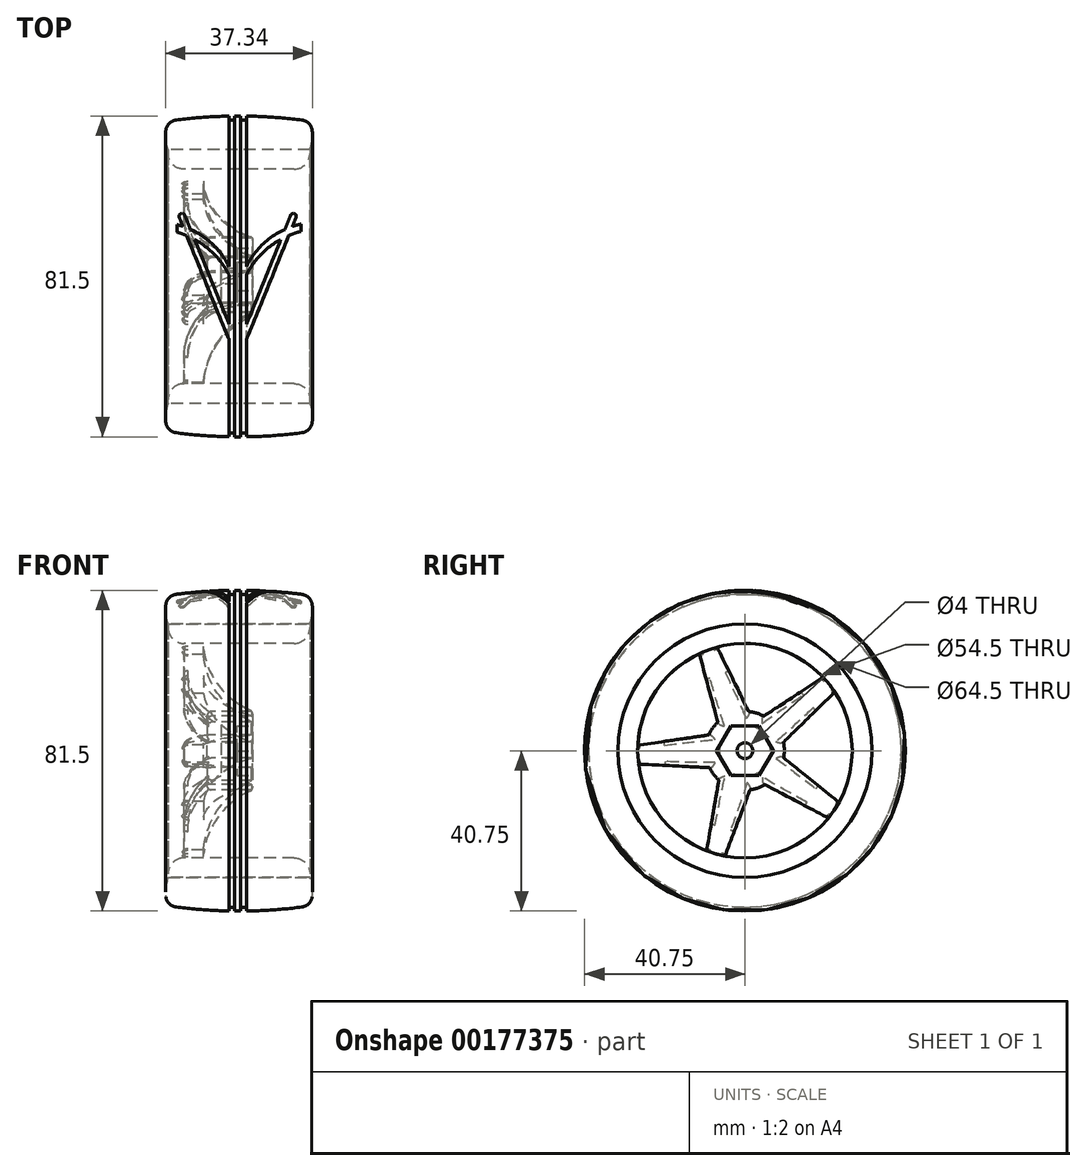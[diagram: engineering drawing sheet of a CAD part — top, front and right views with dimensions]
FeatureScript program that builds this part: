
annotation { "Feature Type Name" : "Feature", "Feature Type Description" : "" }
export const myFeature = defineFeature(function(context is Context, id is Id, definition is map)
    precondition{}
    {
        {
            var Q0;
            Q0=qCreatedBy(makeId("Front.planeOp"),FACE);
            var sketch = newSketch(context, id + "F0", { "sketchPlane" : qUnion([Q0])});
            skLineSegment(sketch, "E0", {"start": v(0, 0) * mm, "end": v(0, 27.25) * mm, "construction": true});
            skLineSegment(sketch, "E1", {"start": v(0, 27.25) * mm, "end": v(18.55, 27.25) * mm, "construction": true});
            skLineSegment(sketch, "E2", {"start": v(18.55, 27.25) * mm, "end": v(18.55, 32.25) * mm, "construction": true});
            skLineSegment(sketch, "E3", {"start": v(18.55, 32.25) * mm, "end": v(-17.45, 32.25) * mm, "construction": true});
            skLineSegment(sketch, "E4", {"start": v(-17.45, 32.25) * mm, "end": v(-17.45, 27.25) * mm, "construction": true});
            skLineSegment(sketch, "E5", {"start": v(-17.45, 27.25) * mm, "end": v(-4, 27.25) * mm, "construction": true});
            skLineSegment(sketch, "E6", {"start": v(-4, 27.25) * mm, "end": v(-4, 0) * mm, "construction": true});
            skLineSegment(sketch, "E7", {"start": v(-4, 0) * mm, "end": v(0, 0) * mm, "construction": true});
            skSolve(sketch);
        }
        {
            var Q0;
            Q0=qCreatedBy(makeId("Front.planeOp"),FACE);
            var sketch = newSketch(context, id + "F1", { "sketchPlane" : qUnion([Q0])});
            skLineSegment(sketch, "E8", {"start": v(-20, 0) * mm, "end": v(20, 0) * mm, "construction": true});
            skLineSegment(sketch, "E9", {"start": v(-4, 2) * mm, "end": v(0, 2) * mm});
            skLineSegment(sketch, "E10", {"start": v(0, 2) * mm, "end": v(0, 6.5) * mm, "construction": true});
            skLineSegment(sketch, "E11", {"start": v(0, 6.5) * mm, "end": v(-4, 6.5) * mm, "construction": true});
            skLineSegment(sketch, "E12", {"start": v(-4, 6.5) * mm, "end": v(-4, 2) * mm});
            skLineSegment(sketch, "E13", {"start": v(-13.45, 27.25) * mm, "end": v(-13.45, 20.44) * mm});
            skArc(sketch, "E14", {"start": v(-13.45, 20.44) * mm, "mid": v(-10.86, 12.02) * mm, "end": v(-4, 6.5) * mm});
            skArc(sketch, "E15", {"start": v(-17.45, 31.25) * mm, "mid": v(-16.28, 28.42) * mm, "end": v(-13.45, 27.25) * mm});
            skLineSegment(sketch, "E16", {"start": v(-17.45, 31.25) * mm, "end": v(-17.45, 32.25) * mm});
            skLineSegment(sketch, "E17", {"start": v(-17.45, 32.25) * mm, "end": v(18.55, 32.25) * mm});
            skLineSegment(sketch, "E18", {"start": v(18.55, 32.25) * mm, "end": v(18.55, 31.25) * mm});
            skLineSegment(sketch, "E19", {"start": v(14.55, 27.25) * mm, "end": v(-8.45, 27.25) * mm});
            skArc(sketch, "E20", {"start": v(-8.45, 27.25) * mm, "mid": v(-4.9, 17.1) * mm, "end": v(3.4, 10.25) * mm});
            skPoint(sketch, "E21.visualSharp", {"position": v(18.55, 27.25) * mm});
            skArc(sketch, "E21.filletArc", {"start": v(14.55, 27.25) * mm, "mid": v(17.38, 28.42) * mm, "end": v(18.55, 31.25) * mm});
            skLineSegment(sketch, "E22", {"start": v(4, 9.34) * mm, "end": v(4, 3) * mm});
            skLineSegment(sketch, "E23", {"start": v(4, 3) * mm, "end": v(0, 3) * mm});
            skLineSegment(sketch, "E24", {"start": v(0, 3) * mm, "end": v(0, 2) * mm});
            skPoint(sketch, "E25.visualSharp", {"position": v(4, 10) * mm});
            skArc(sketch, "E25.filletArc", {"start": v(4, 9.34) * mm, "mid": v(3.84, 9.88) * mm, "end": v(3.4, 10.25) * mm});
            skSolve(sketch);
        }
        {
            var Q0;
            Q0=qSketchRegion(id+"F1",true);
            var Q1;
            Q1=sQuery(id+"F1.wireOp",EDGE,"E8");
            revolve(context, id + "F2", {"surfaceOperationType" : NewSurfaceOperationType.NEW, "entities" : qUnion([Q0]), "axis" : qUnion([Q1]), "revolveType" : RevolveType.FULL});
        }
        {
            var Q0;
            Q0=makeQuery(id+"F2.opRevolve","SWEPT_FACE",FACE,{"disambiguationData":[OSD([sQuery(id+"F1.wireOp",EDGE,"E22")])]});
            var sketch = newSketch(context, id + "F3", { "sketchPlane" : qUnion([Q0])});
            skCircle(sketch, "E26.cCircle", {"center": v(0, 0) * mm, "radius": 6.25 * mm, "construction": true});
            skLineSegment(sketch, "E26.0", {"start": v(-3.6, 6.25) * mm, "end": v(3.6, 6.25) * mm});
            skLineSegment(sketch, "E26.1", {"start": v(3.6, 6.25) * mm, "end": v(7.22, 0) * mm});
            skLineSegment(sketch, "E26.2", {"start": v(7.22, 0) * mm, "end": v(3.6, -6.25) * mm});
            skLineSegment(sketch, "E26.3", {"start": v(3.6, -6.25) * mm, "end": v(-3.6, -6.25) * mm});
            skLineSegment(sketch, "E26.4", {"start": v(-3.6, -6.25) * mm, "end": v(-7.22, 0) * mm});
            skLineSegment(sketch, "E26.5", {"start": v(-7.22, 0) * mm, "end": v(-3.6, 6.25) * mm});
            skPoint(sketch, "E26.0.midPoint", {"position": v(0, 6.25) * mm});
            skSolve(sketch);
        }
        {
            var Q0;
            Q0=qSketchRegion(id+"F3",true);
            var Q1;
            Q1=makeQuery(id+"F2.opRevolve","SWEPT_FACE",FACE,{"disambiguationData":[OSD([sQuery(id+"F1.wireOp",EDGE,"E24")])]});
            extrude(context, id + "F4", {"entities" : qUnion([Q0]), "operationType" : NewBodyOperationType.REMOVE, "endBound" : BoundingType.UP_TO_SURFACE, "oppositeDirection" : true, "depth" : 25 * mm, "endBoundEntityFace" : qUnion([Q1]), "offsetDistance" : 25 * mm});
        }
        {
            var Q0;
            Q0=makeQuery(id+"F2.opRevolve","SWEPT_FACE",FACE,{"disambiguationData":[OSD([sQuery(id+"F1.wireOp",EDGE,"E16")])]});
            var sketch = newSketch(context, id + "F5", { "sketchPlane" : qUnion([Q0])});
            skLineSegment(sketch, "E27", {"start": v(11.62, 24.65) * mm, "end": v(6.88, 7.26) * mm});
            skArc(sketch, "E28", {"start": v(9.17, 3.98) * mm, "mid": v(8.2, 5.74) * mm, "end": v(6.88, 7.26) * mm});
            skLineSegment(sketch, "E29", {"start": v(9.17, 3.98) * mm, "end": v(27.21, 1.4) * mm});
            skArc(sketch, "E30", {"start": v(27.21, 1.4) * mm, "mid": v(22.63, 15.18) * mm, "end": v(11.62, 24.65) * mm});
            skLineSegment(sketch, "E31", {"start": v(0, 0) * mm, "end": v(22.32, 15.63) * mm, "construction": true});
            skLineSegment(sketch, "E32.1.0", {"start": v(-19.85, 18.66) * mm, "end": v(-4.78, 8.79) * mm});
            skArc(sketch, "E32.1.1", {"start": v(7.08, 26.31) * mm, "mid": v(-7.44, 26.21) * mm, "end": v(-19.85, 18.66) * mm});
            skLineSegment(sketch, "E32.1.2", {"start": v(-0.95, 9.95) * mm, "end": v(7.08, 26.31) * mm});
            skArc(sketch, "E32.1.3", {"start": v(-0.95, 9.95) * mm, "mid": v(-2.92, 9.56) * mm, "end": v(-4.78, 8.79) * mm});
            skLineSegment(sketch, "E32.2.0", {"start": v(-23.89, -13.12) * mm, "end": v(-9.83, -1.83) * mm});
            skArc(sketch, "E32.2.1", {"start": v(-22.84, 14.87) * mm, "mid": v(-27.23, 1.02) * mm, "end": v(-23.89, -13.12) * mm});
            skLineSegment(sketch, "E32.2.2", {"start": v(-9.76, 2.17) * mm, "end": v(-22.84, 14.87) * mm});
            skArc(sketch, "E32.2.3", {"start": v(-9.76, 2.17) * mm, "mid": v(-10, 0.17) * mm, "end": v(-9.83, -1.83) * mm});
            skLineSegment(sketch, "E32.3.0", {"start": v(5.1, -26.77) * mm, "end": v(-1.3, -9.92) * mm});
            skArc(sketch, "E32.3.1", {"start": v(-21.2, -17.13) * mm, "mid": v(-9.38, -25.58) * mm, "end": v(5.1, -26.77) * mm});
            skLineSegment(sketch, "E32.3.2", {"start": v(-5.08, -8.61) * mm, "end": v(-21.2, -17.13) * mm});
            skArc(sketch, "E32.3.3", {"start": v(-5.08, -8.61) * mm, "mid": v(-3.26, -9.46) * mm, "end": v(-1.3, -9.92) * mm});
            skLineSegment(sketch, "E32.4.0", {"start": v(27.03, -3.43) * mm, "end": v(9.03, -4.3) * mm});
            skArc(sketch, "E32.4.1", {"start": v(9.74, -25.45) * mm, "mid": v(21.43, -16.83) * mm, "end": v(27.03, -3.43) * mm});
            skLineSegment(sketch, "E32.4.2", {"start": v(6.62, -7.5) * mm, "end": v(9.74, -25.45) * mm});
            skArc(sketch, "E32.4.3", {"start": v(6.62, -7.5) * mm, "mid": v(7.99, -6.02) * mm, "end": v(9.03, -4.3) * mm});
            skSolve(sketch);
        }
        {
            var Q0;
            Q0=qSketchRegion(id+"F5",true);
            extrude(context, id + "F6", {"entities" : qUnion([Q0]), "operationType" : NewBodyOperationType.REMOVE, "endBound" : BoundingType.THROUGH_ALL, "oppositeDirection" : true, "depth" : 25 * mm, "offsetDistance" : 25 * mm});
        }
        {
            var Q0;
            Q0=makeQuery(id+"F6.boolean.opBoolean","INTERSECT",EDGE,{"derivedFrom":[makeQuery(id+"F2.opRevolve","SWEPT_FACE",FACE,{"disambiguationData":[OSD([sQuery(id+"F1.wireOp",EDGE,"E14")])]}),makeQuery(id+"F6.opExtrude","SWEPT_FACE",FACE,{"disambiguationData":[OSD([sQuery(id+"F5.wireOp",EDGE,"E32.2.0")])]})]});
            var Q1;
            Q1=makeQuery(id+"F6.boolean.opBoolean","INTERSECT",EDGE,{"derivedFrom":[makeQuery(id+"F2.opRevolve","SWEPT_FACE",FACE,{"disambiguationData":[OSD([sQuery(id+"F1.wireOp",EDGE,"E13")])]}),makeQuery(id+"F6.opExtrude","SWEPT_FACE",FACE,{"disambiguationData":[OSD([sQuery(id+"F5.wireOp",EDGE,"E32.3.2")])]})]});
            var Q2;
            Q2=makeQuery(id+"F6.boolean.opBoolean","INTERSECT",EDGE,{"derivedFrom":[makeQuery(id+"F2.opRevolve","SWEPT_FACE",FACE,{"disambiguationData":[OSD([sQuery(id+"F1.wireOp",EDGE,"E14")])]}),makeQuery(id+"F6.opExtrude","SWEPT_FACE",FACE,{"disambiguationData":[OSD([sQuery(id+"F5.wireOp",EDGE,"E32.3.3")])]})]});
            var Q3;
            Q3=makeQuery(id+"F6.boolean.opBoolean","INTERSECT",EDGE,{"derivedFrom":[makeQuery(id+"F2.opRevolve","SWEPT_FACE",FACE,{"disambiguationData":[OSD([sQuery(id+"F1.wireOp",EDGE,"E14")])]}),makeQuery(id+"F6.opExtrude","SWEPT_FACE",FACE,{"disambiguationData":[OSD([sQuery(id+"F5.wireOp",EDGE,"E32.2.3")])]})]});
            var Q4;
            Q4=makeQuery(id+"F6.boolean.opBoolean","INTERSECT",EDGE,{"derivedFrom":[makeQuery(id+"F2.opRevolve","SWEPT_FACE",FACE,{"disambiguationData":[OSD([sQuery(id+"F1.wireOp",EDGE,"E14")])]}),makeQuery(id+"F6.opExtrude","SWEPT_FACE",FACE,{"disambiguationData":[OSD([sQuery(id+"F5.wireOp",EDGE,"E32.2.2")])]})]});
            var Q5;
            Q5=makeQuery(id+"F6.boolean.opBoolean","INTERSECT",EDGE,{"derivedFrom":[makeQuery(id+"F2.opRevolve","SWEPT_FACE",FACE,{"disambiguationData":[OSD([sQuery(id+"F1.wireOp",EDGE,"E14")])]}),makeQuery(id+"F6.opExtrude","SWEPT_FACE",FACE,{"disambiguationData":[OSD([sQuery(id+"F5.wireOp",EDGE,"E32.1.3")])]})]});
            var Q6;
            Q6=makeQuery(id+"F6.boolean.opBoolean","INTERSECT",EDGE,{"derivedFrom":[makeQuery(id+"F2.opRevolve","SWEPT_FACE",FACE,{"disambiguationData":[OSD([sQuery(id+"F1.wireOp",EDGE,"E14")])]}),makeQuery(id+"F6.opExtrude","SWEPT_FACE",FACE,{"disambiguationData":[OSD([sQuery(id+"F5.wireOp",EDGE,"E32.1.0")])]})]});
            var Q7;
            Q7=makeQuery(id+"F6.boolean.opBoolean","INTERSECT",EDGE,{"derivedFrom":[makeQuery(id+"F2.opRevolve","SWEPT_FACE",FACE,{"disambiguationData":[OSD([sQuery(id+"F1.wireOp",EDGE,"E14")])]}),makeQuery(id+"F6.opExtrude","SWEPT_FACE",FACE,{"disambiguationData":[OSD([sQuery(id+"F5.wireOp",EDGE,"E32.3.0")])]})]});
            var Q8;
            Q8=makeQuery(id+"F6.boolean.opBoolean","INTERSECT",EDGE,{"derivedFrom":[makeQuery(id+"F2.opRevolve","SWEPT_FACE",FACE,{"disambiguationData":[OSD([sQuery(id+"F1.wireOp",EDGE,"E14")])]}),makeQuery(id+"F6.opExtrude","SWEPT_FACE",FACE,{"disambiguationData":[OSD([sQuery(id+"F5.wireOp",EDGE,"E32.4.2")])]})]});
            var Q9;
            Q9=makeQuery(id+"F6.boolean.opBoolean","INTERSECT",EDGE,{"derivedFrom":[makeQuery(id+"F2.opRevolve","SWEPT_FACE",FACE,{"disambiguationData":[OSD([sQuery(id+"F1.wireOp",EDGE,"E14")])]}),makeQuery(id+"F6.opExtrude","SWEPT_FACE",FACE,{"disambiguationData":[OSD([sQuery(id+"F5.wireOp",EDGE,"E32.4.3")])]})]});
            var Q10;
            Q10=makeQuery(id+"F6.boolean.opBoolean","INTERSECT",EDGE,{"derivedFrom":[makeQuery(id+"F2.opRevolve","SWEPT_FACE",FACE,{"disambiguationData":[OSD([sQuery(id+"F1.wireOp",EDGE,"E14")])]}),makeQuery(id+"F6.opExtrude","SWEPT_FACE",FACE,{"disambiguationData":[OSD([sQuery(id+"F5.wireOp",EDGE,"E32.4.0")])]})]});
            var Q11;
            Q11=makeQuery(id+"F6.boolean.opBoolean","INTERSECT",EDGE,{"derivedFrom":[makeQuery(id+"F2.opRevolve","SWEPT_FACE",FACE,{"disambiguationData":[OSD([sQuery(id+"F1.wireOp",EDGE,"E14")])]}),makeQuery(id+"F6.opExtrude","SWEPT_FACE",FACE,{"disambiguationData":[OSD([sQuery(id+"F5.wireOp",EDGE,"E29")])]})]});
            var Q12;
            Q12=makeQuery(id+"F6.boolean.opBoolean","INTERSECT",EDGE,{"derivedFrom":[makeQuery(id+"F2.opRevolve","SWEPT_FACE",FACE,{"disambiguationData":[OSD([sQuery(id+"F1.wireOp",EDGE,"E14")])]}),makeQuery(id+"F6.opExtrude","SWEPT_FACE",FACE,{"disambiguationData":[OSD([sQuery(id+"F5.wireOp",EDGE,"E28")])]})]});
            var Q13;
            Q13=makeQuery(id+"F6.boolean.opBoolean","INTERSECT",EDGE,{"derivedFrom":[makeQuery(id+"F2.opRevolve","SWEPT_FACE",FACE,{"disambiguationData":[OSD([sQuery(id+"F1.wireOp",EDGE,"E14")])]}),makeQuery(id+"F6.opExtrude","SWEPT_FACE",FACE,{"disambiguationData":[OSD([sQuery(id+"F5.wireOp",EDGE,"E27")])]})]});
            var Q14;
            Q14=makeQuery(id+"F6.boolean.opBoolean","INTERSECT",EDGE,{"derivedFrom":[makeQuery(id+"F2.opRevolve","SWEPT_FACE",FACE,{"disambiguationData":[OSD([sQuery(id+"F1.wireOp",EDGE,"E14")])]}),makeQuery(id+"F6.opExtrude","SWEPT_FACE",FACE,{"disambiguationData":[OSD([sQuery(id+"F5.wireOp",EDGE,"E32.1.2")])]})]});
            fillet(context, id + "F7", {"entities" : qUnion([Q0, Q1, Q2, Q3, Q4, Q5, Q6, Q7, Q8, Q9, Q10, Q11, Q12, Q13, Q14]), "radius" : 1 * mm, "tangentPropagation" : true, "allowEdgeOverflow" : false});
        }
        {
            var Q0;
            Q0=makeQuery(id+"F6.boolean.opBoolean","COPY",EDGE,{"derivedFrom":makeQuery(id+"F6.opExtrude","SWEPT_EDGE",EDGE,{"disambiguationData":[OSD([sQuery(id+"F5.wireOp",EDGE,"E32.2.1"),sQuery(id+"F5.wireOp",EDGE,"E32.2.2")])]})});
            var Q1;
            Q1=makeQuery(id+"F6.boolean.opBoolean","COPY",EDGE,{"derivedFrom":makeQuery(id+"F6.opExtrude","SWEPT_EDGE",EDGE,{"disambiguationData":[OSD([sQuery(id+"F5.wireOp",EDGE,"E27"),sQuery(id+"F5.wireOp",EDGE,"E30")])]})});
            var Q2;
            Q2=makeQuery(id+"F6.boolean.opBoolean","COPY",EDGE,{"derivedFrom":makeQuery(id+"F6.opExtrude","SWEPT_EDGE",EDGE,{"disambiguationData":[OSD([sQuery(id+"F5.wireOp",EDGE,"E32.4.0"),sQuery(id+"F5.wireOp",EDGE,"E32.4.1")])]})});
            var Q3;
            Q3=makeQuery(id+"F6.boolean.opBoolean","COPY",EDGE,{"derivedFrom":makeQuery(id+"F6.opExtrude","SWEPT_EDGE",EDGE,{"disambiguationData":[OSD([sQuery(id+"F5.wireOp",EDGE,"E32.4.1"),sQuery(id+"F5.wireOp",EDGE,"E32.4.2")])]})});
            var Q4;
            Q4=makeQuery(id+"F6.boolean.opBoolean","COPY",EDGE,{"derivedFrom":makeQuery(id+"F6.opExtrude","SWEPT_EDGE",EDGE,{"disambiguationData":[OSD([sQuery(id+"F5.wireOp",EDGE,"E32.2.0"),sQuery(id+"F5.wireOp",EDGE,"E32.2.1")])]})});
            fillet(context, id + "F8", {"entities" : qUnion([Q0, Q1, Q2, Q3, Q4]), "radius" : 0.5 * mm, "tangentPropagation" : true, "allowEdgeOverflow" : false});
        }
        {
            var Q0;
            Q0=qCreatedBy(makeId("Front.planeOp"),FACE);
            var sketch = newSketch(context, id + "F9", { "sketchPlane" : qUnion([Q0])});
            skLineSegment(sketch, "E33", {"start": v(39.81, 0) * mm, "end": v(-23.66, 0) * mm, "construction": true});
            skArc(sketch, "E34", {"start": v(16.55, 39.72) * mm, "mid": v(0.55, 40.75) * mm, "end": v(-15.45, 39.72) * mm});
            skArc(sketch, "E35", {"start": v(-18.04, 37.13) * mm, "mid": v(-18.05, 34.65) * mm, "end": v(-17.45, 32.25) * mm});
            skArc(sketch, "E36", {"start": v(18.55, 32.25) * mm, "mid": v(19.15, 34.65) * mm, "end": v(19.14, 37.13) * mm});
            skLineSegment(sketch, "E37", {"start": v(18.55, 32.25) * mm, "end": v(-17.45, 32.25) * mm});
            skPoint(sketch, "E38.visualSharp", {"position": v(18.55, 39.45) * mm});
            skArc(sketch, "E38.filletArc", {"start": v(19.14, 37.13) * mm, "mid": v(18.28, 38.87) * mm, "end": v(16.55, 39.72) * mm});
            skPoint(sketch, "E39.visualSharp", {"position": v(-17.45, 39.45) * mm});
            skArc(sketch, "E39.filletArc", {"start": v(-15.45, 39.72) * mm, "mid": v(-17.18, 38.87) * mm, "end": v(-18.04, 37.13) * mm});
            skSolve(sketch);
        }
        {
            var Q0;
            Q0=qSketchRegion(id+"F9",true);
            var Q1;
            Q1=sQuery(id+"F9.wireOp",EDGE,"E33");
            revolve(context, id + "F10", {"surfaceOperationType" : NewSurfaceOperationType.NEW, "entities" : qUnion([Q0]), "axis" : qUnion([Q1]), "revolveType" : RevolveType.FULL});
        }
        {
            var Q0;
            Q0=qCreatedBy(makeId("Front.planeOp"),FACE);
            var sketch = newSketch(context, id + "F11", { "sketchPlane" : qUnion([Q0])});
            skLineSegment(sketch, "E40", {"start": v(-0.54, 41.75) * mm, "end": v(-0.54, 39.75) * mm});
            skLineSegment(sketch, "E41", {"start": v(-2.04, 39.75) * mm, "end": v(-2.04, 41.75) * mm});
            skLineSegment(sketch, "E42", {"start": v(-2.04, 41.75) * mm, "end": v(-0.54, 41.75) * mm});
            skLineSegment(sketch, "E43", {"start": v(2.46, 41.75) * mm, "end": v(2.46, 39.75) * mm});
            skLineSegment(sketch, "E44", {"start": v(0.96, 39.75) * mm, "end": v(0.96, 41.75) * mm});
            skLineSegment(sketch, "E45", {"start": v(0.96, 41.75) * mm, "end": v(2.46, 41.75) * mm});
            skLineSegment(sketch, "E46", {"start": v(2.46, 39.75) * mm, "end": v(0.96, 39.75) * mm});
            skLineSegment(sketch, "E47", {"start": v(-0.54, 39.75) * mm, "end": v(-2.04, 39.75) * mm});
            skLineSegment(sketch, "E48", {"start": v(0, 0) * mm, "end": v(-18.32, 0) * mm, "construction": true});
            skSolve(sketch);
        }
        {
            var Q0;
            Q0=qSketchRegion(id+"F11",true);
            var Q1;
            Q1=makeQuery(id+"F10.opRevolve","SWEPT_FACE",FACE,{"disambiguationData":[OSD([sQuery(id+"F9.wireOp",EDGE,"E34")])]});
            revolve(context, id + "F12", {"operationType" : NewBodyOperationType.REMOVE, "surfaceOperationType" : NewSurfaceOperationType.NEW, "entities" : qUnion([Q0]), "axis" : qUnion([Q1]), "revolveType" : RevolveType.FULL, "oppositeDirection" : true});
        }
        {
            var Q0;
            Q0=qCreatedBy(makeId("Top.planeOp"),FACE);
            cPlane(context, id + "F13", {"entities" : qUnion([Q0]), "cplaneType" : CPlaneType.OFFSET, "offset" : 42.75 * mm, "width" : 150 * mm, "height" : 150 * mm});
        }
        {
            var Q0;
            Q0=qCreatedBy(id+"F13.planeOp",FACE);
            var sketch = newSketch(context, id + "F14", { "sketchPlane" : qUnion([Q0])});
            skLineSegment(sketch, "E49", {"start": v(-1.79, 0) * mm, "end": v(-1.79, 2) * mm});
            skArc(sketch, "E50", {"start": v(-1.79, 2) * mm, "mid": v(-10.48, 11.32) * mm, "end": v(-23.04, 13.5) * mm});
            skArc(sketch, "E51", {"start": v(-1.79, 0) * mm, "mid": v(-10.54, 9.3) * mm, "end": v(-23.04, 12) * mm});
            skLineSegment(sketch, "E52", {"start": v(-23.04, 12) * mm, "end": v(-23.04, 13.5) * mm});
            skLineSegment(sketch, "E53", {"start": v(0.21, 6.52) * mm, "end": v(0.21, -6.35) * mm, "construction": true});
            skArc(sketch, "E54.MirrorCS", {"start": v(2.21, 0) * mm, "mid": v(10.97, 9.3) * mm, "end": v(23.46, 12) * mm});
            skArc(sketch, "E55.MirrorCS", {"start": v(2.21, 2) * mm, "mid": v(10.9, 11.32) * mm, "end": v(23.46, 13.5) * mm});
            skLineSegment(sketch, "E56.MirrorCS", {"start": v(23.46, 12) * mm, "end": v(23.46, 13.5) * mm});
            skLineSegment(sketch, "E57.MirrorCS", {"start": v(2.21, 0) * mm, "end": v(2.21, 2) * mm});
            skSolve(sketch);
        }
        {
            var Q0;
            Q0=qSketchRegion(id+"F14",true);
            var Q1;
            Q1=makeQuery(id+"F12.boolean.opBoolean","COPY",FACE,{"derivedFrom":makeQuery(id+"F12.opRevolve","SWEPT_FACE",FACE,{"disambiguationData":[OSD([sQuery(id+"F11.wireOp",EDGE,"E46")])]})});
            extrude(context, id + "F15", {"entities" : qUnion([Q0]), "operationType" : NewBodyOperationType.REMOVE, "endBound" : BoundingType.UP_TO_SURFACE, "oppositeDirection" : true, "depth" : 25 * mm, "endBoundEntityFace" : qUnion([Q1]), "offsetDistance" : 25 * mm});
        }
        {
            var Q0;
            Q0=qCreatedBy(id+"F13.planeOp",FACE);
            var sketch = newSketch(context, id + "F16", { "sketchPlane" : qUnion([Q0])});
            skLineSegment(sketch, "E58", {"start": v(1.27, -15) * mm, "end": v(13.66, 15.56) * mm});
            skLineSegment(sketch, "E59", {"start": v(13.66, 15.56) * mm, "end": v(15.05, 15) * mm, "construction": true});
            skLineSegment(sketch, "E60", {"start": v(15.05, 15) * mm, "end": v(2.66, -15.56) * mm});
            skLineSegment(sketch, "E61", {"start": v(2.66, -15.56) * mm, "end": v(1.27, -15) * mm, "construction": true});
            skArc(sketch, "E62", {"start": v(15.05, 15) * mm, "mid": v(14.63, 15.98) * mm, "end": v(13.66, 15.56) * mm});
            skArc(sketch, "E63", {"start": v(1.27, -15) * mm, "mid": v(1.68, -15.98) * mm, "end": v(2.66, -15.56) * mm});
            skLineSegment(sketch, "E64", {"start": v(0.21, 11.65) * mm, "end": v(0.21, -13.65) * mm, "construction": true});
            skLineSegment(sketch, "E65.MirrorCS", {"start": v(-0.84, -15) * mm, "end": v(-13.23, 15.56) * mm});
            skLineSegment(sketch, "E66.MirrorCS", {"start": v(-14.62, 15) * mm, "end": v(-2.23, -15.56) * mm});
            skArc(sketch, "E67.MirrorCS", {"start": v(-14.62, 15) * mm, "mid": v(-14.2, 15.98) * mm, "end": v(-13.23, 15.56) * mm});
            skArc(sketch, "E68.MirrorCS", {"start": v(-0.84, -15) * mm, "mid": v(-1.26, -15.98) * mm, "end": v(-2.23, -15.56) * mm});
            skSolve(sketch);
        }
        {
            var Q0;
            Q0=makeQuery(id+"F16.imprint","IMPRINT",FACE,{"disambiguationData":[TD([[makeQuery(id+"F16.imprint","IMPRINT",EDGE,{"derivedFrom":sQuery(id+"F16.wireOp",EDGE,"E58")}),-1.0]])]});
            var Q1;
            Q1=makeQuery(id+"F16.imprint","IMPRINT",FACE,{"disambiguationData":[TD([[makeQuery(id+"F16.imprint","IMPRINT",EDGE,{"derivedFrom":sQuery(id+"F16.wireOp",EDGE,"E65.MirrorCS")}),1.0]])]});
            var Q2;
            {var subQ0=sQuery(id+"F14.wireOp",EDGE,"E57.MirrorCS");var subQ1=sQuery(id+"F14.wireOp",EDGE,"E56.MirrorCS");var subQ2=sQuery(id+"F14.wireOp",EDGE,"E55.MirrorCS");var subQ3=sQuery(id+"F14.wireOp",EDGE,"E54.MirrorCS");Q2=makeQuery(id+"FRkk9yGD8DPVHCN_2.23.F15.boolean.opBoolean","MERGE",FACE,{"derivedFrom":[makeQuery(id+"FRkk9yGD8DPVHCN_2.22.F15.boolean.opBoolean","MERGE",FACE,{"derivedFrom":[makeQuery(id+"FRkk9yGD8DPVHCN_2.21.F15.boolean.opBoolean","MERGE",FACE,{"derivedFrom":[makeQuery(id+"FRkk9yGD8DPVHCN_2.20.F15.boolean.opBoolean","MERGE",FACE,{"derivedFrom":[makeQuery(id+"FRkk9yGD8DPVHCN_2.19.F15.boolean.opBoolean","MERGE",FACE,{"derivedFrom":[makeQuery(id+"FRkk9yGD8DPVHCN_2.18.F15.boolean.opBoolean","MERGE",FACE,{"derivedFrom":[makeQuery(id+"FRkk9yGD8DPVHCN_2.17.F15.boolean.opBoolean","MERGE",FACE,{"derivedFrom":[makeQuery(id+"FRkk9yGD8DPVHCN_2.16.F15.boolean.opBoolean","MERGE",FACE,{"derivedFrom":[makeQuery(id+"FRkk9yGD8DPVHCN_2.15.F15.boolean.opBoolean","MERGE",FACE,{"derivedFrom":[makeQuery(id+"FRkk9yGD8DPVHCN_2.14.F15.boolean.opBoolean","MERGE",FACE,{"derivedFrom":[makeQuery(id+"FRkk9yGD8DPVHCN_2.13.F15.boolean.opBoolean","MERGE",FACE,{"derivedFrom":[makeQuery(id+"FRkk9yGD8DPVHCN_2.12.F15.boolean.opBoolean","MERGE",FACE,{"derivedFrom":[makeQuery(id+"FRkk9yGD8DPVHCN_2.11.F15.boolean.opBoolean","MERGE",FACE,{"derivedFrom":[makeQuery(id+"FRkk9yGD8DPVHCN_2.10.F15.boolean.opBoolean","MERGE",FACE,{"derivedFrom":[makeQuery(id+"FRkk9yGD8DPVHCN_2.9.F15.boolean.opBoolean","MERGE",FACE,{"derivedFrom":[makeQuery(id+"FRkk9yGD8DPVHCN_2.8.F15.boolean.opBoolean","MERGE",FACE,{"derivedFrom":[makeQuery(id+"FRkk9yGD8DPVHCN_2.7.F15.boolean.opBoolean","MERGE",FACE,{"derivedFrom":[makeQuery(id+"FRkk9yGD8DPVHCN_2.6.F15.boolean.opBoolean","MERGE",FACE,{"derivedFrom":[makeQuery(id+"FRkk9yGD8DPVHCN_2.5.F15.boolean.opBoolean","MERGE",FACE,{"derivedFrom":[makeQuery(id+"FRkk9yGD8DPVHCN_2.4.F15.boolean.opBoolean","MERGE",FACE,{"derivedFrom":[makeQuery(id+"FRkk9yGD8DPVHCN_2.3.F15.boolean.opBoolean","MERGE",FACE,{"derivedFrom":[makeQuery(id+"FRkk9yGD8DPVHCN_2.2.F15.boolean.opBoolean","MERGE",FACE,{"derivedFrom":[makeQuery(id+"FRkk9yGD8DPVHCN_2.1.F15.boolean.opBoolean","MERGE",FACE,{"derivedFrom":[makeQuery(id+"F15.boolean.opBoolean","MERGE",FACE,{"derivedFrom":[makeQuery(id+"F12.boolean.opBoolean","COPY",FACE,{"derivedFrom":makeQuery(id+"F12.opRevolve","SWEPT_FACE",FACE,{"disambiguationData":[OSD([sQuery(id+"F11.wireOp",EDGE,"E46")])]})})],"fromTools":[makeQuery(id+"F15.opExtrude","CAP_FACE",FACE,{"disambiguationData":[OSD([subQ3,subQ2,subQ1,subQ0])],"isStart":false})]})],"fromTools":[makeQuery(id+"FRkk9yGD8DPVHCN_2.1.F15.opExtrude","CAP_FACE",FACE,{"disambiguationData":[OSD([subQ3,subQ2,subQ1,subQ0])],"isStart":false})]})],"fromTools":[makeQuery(id+"FRkk9yGD8DPVHCN_2.2.F15.opExtrude","CAP_FACE",FACE,{"disambiguationData":[OSD([subQ3,subQ2,subQ1,subQ0])],"isStart":false})]})],"fromTools":[makeQuery(id+"FRkk9yGD8DPVHCN_2.3.F15.opExtrude","CAP_FACE",FACE,{"disambiguationData":[OSD([subQ3,subQ2,subQ1,subQ0])],"isStart":false})]})],"fromTools":[makeQuery(id+"FRkk9yGD8DPVHCN_2.4.F15.opExtrude","CAP_FACE",FACE,{"disambiguationData":[OSD([subQ3,subQ2,subQ1,subQ0])],"isStart":false})]})],"fromTools":[makeQuery(id+"FRkk9yGD8DPVHCN_2.5.F15.opExtrude","CAP_FACE",FACE,{"disambiguationData":[OSD([subQ3,subQ2,subQ1,subQ0])],"isStart":false})]})],"fromTools":[makeQuery(id+"FRkk9yGD8DPVHCN_2.6.F15.opExtrude","CAP_FACE",FACE,{"disambiguationData":[OSD([subQ3,subQ2,subQ1,subQ0])],"isStart":false})]})],"fromTools":[makeQuery(id+"FRkk9yGD8DPVHCN_2.7.F15.opExtrude","CAP_FACE",FACE,{"disambiguationData":[OSD([subQ3,subQ2,subQ1,subQ0])],"isStart":false})]})],"fromTools":[makeQuery(id+"FRkk9yGD8DPVHCN_2.8.F15.opExtrude","CAP_FACE",FACE,{"disambiguationData":[OSD([subQ3,subQ2,subQ1,subQ0])],"isStart":false})]})],"fromTools":[makeQuery(id+"FRkk9yGD8DPVHCN_2.9.F15.opExtrude","CAP_FACE",FACE,{"disambiguationData":[OSD([subQ3,subQ2,subQ1,subQ0])],"isStart":false})]})],"fromTools":[makeQuery(id+"FRkk9yGD8DPVHCN_2.10.F15.opExtrude","CAP_FACE",FACE,{"disambiguationData":[OSD([subQ3,subQ2,subQ1,subQ0])],"isStart":false})]})],"fromTools":[makeQuery(id+"FRkk9yGD8DPVHCN_2.11.F15.opExtrude","CAP_FACE",FACE,{"disambiguationData":[OSD([subQ3,subQ2,subQ1,subQ0])],"isStart":false})]})],"fromTools":[makeQuery(id+"FRkk9yGD8DPVHCN_2.12.F15.opExtrude","CAP_FACE",FACE,{"disambiguationData":[OSD([subQ3,subQ2,subQ1,subQ0])],"isStart":false})]})],"fromTools":[makeQuery(id+"FRkk9yGD8DPVHCN_2.13.F15.opExtrude","CAP_FACE",FACE,{"disambiguationData":[OSD([subQ3,subQ2,subQ1,subQ0])],"isStart":false})]})],"fromTools":[makeQuery(id+"FRkk9yGD8DPVHCN_2.14.F15.opExtrude","CAP_FACE",FACE,{"disambiguationData":[OSD([subQ3,subQ2,subQ1,subQ0])],"isStart":false})]})],"fromTools":[makeQuery(id+"FRkk9yGD8DPVHCN_2.15.F15.opExtrude","CAP_FACE",FACE,{"disambiguationData":[OSD([subQ3,subQ2,subQ1,subQ0])],"isStart":false})]})],"fromTools":[makeQuery(id+"FRkk9yGD8DPVHCN_2.16.F15.opExtrude","CAP_FACE",FACE,{"disambiguationData":[OSD([subQ3,subQ2,subQ1,subQ0])],"isStart":false})]})],"fromTools":[makeQuery(id+"FRkk9yGD8DPVHCN_2.17.F15.opExtrude","CAP_FACE",FACE,{"disambiguationData":[OSD([subQ3,subQ2,subQ1,subQ0])],"isStart":false})]})],"fromTools":[makeQuery(id+"FRkk9yGD8DPVHCN_2.18.F15.opExtrude","CAP_FACE",FACE,{"disambiguationData":[OSD([subQ3,subQ2,subQ1,subQ0])],"isStart":false})]})],"fromTools":[makeQuery(id+"FRkk9yGD8DPVHCN_2.19.F15.opExtrude","CAP_FACE",FACE,{"disambiguationData":[OSD([subQ3,subQ2,subQ1,subQ0])],"isStart":false})]})],"fromTools":[makeQuery(id+"FRkk9yGD8DPVHCN_2.20.F15.opExtrude","CAP_FACE",FACE,{"disambiguationData":[OSD([subQ3,subQ2,subQ1,subQ0])],"isStart":false})]})],"fromTools":[makeQuery(id+"FRkk9yGD8DPVHCN_2.21.F15.opExtrude","CAP_FACE",FACE,{"disambiguationData":[OSD([subQ3,subQ2,subQ1,subQ0])],"isStart":false})]})],"fromTools":[makeQuery(id+"FRkk9yGD8DPVHCN_2.22.F15.opExtrude","CAP_FACE",FACE,{"disambiguationData":[OSD([subQ3,subQ2,subQ1,subQ0])],"isStart":false})]})],"fromTools":[makeQuery(id+"FRkk9yGD8DPVHCN_2.23.F15.opExtrude","CAP_FACE",FACE,{"disambiguationData":[OSD([subQ3,subQ2,subQ1,subQ0])],"isStart":false})]});}
            extrude(context, id + "F17", {"entities" : qUnion([Q0, Q1]), "operationType" : NewBodyOperationType.REMOVE, "endBound" : BoundingType.UP_TO_SURFACE, "oppositeDirection" : true, "depth" : 25 * mm, "endBoundEntityFace" : qUnion([Q2]), "offsetDistance" : 25 * mm});
        }
    });
